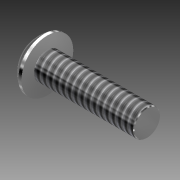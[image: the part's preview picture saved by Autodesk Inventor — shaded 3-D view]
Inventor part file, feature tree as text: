
AUTODESK INVENTOR PART (.ipt)
format: ipt  version: 2012 (Build 160160000, 160)  size: 116,736 bytes
history: native  units: in
note: dims shown in document units (in); Inventor stores cm internally (conversion verified against a paired STEP export)
features: other x1, imported_body x1, thread x1
ambient origin geometry x8: Origin, YZ Plane, XZ Plane, XY Plane, X Axis, Y Axis, Z Axis, Center Point
feature tree (3):
  parser-record x1  (decoder bookkeeping rows leaked as tree rows — omitted from the tree; the rows remain in map.json)
  imported_body  "Base1"
  thread  "Thread1"  [1 undecoded]
note: 1 required parameter value undecoded (feature->parameter linkage not recoverable at this tier; creation-order binding heuristic only, values carry confidence <= 0.55)
